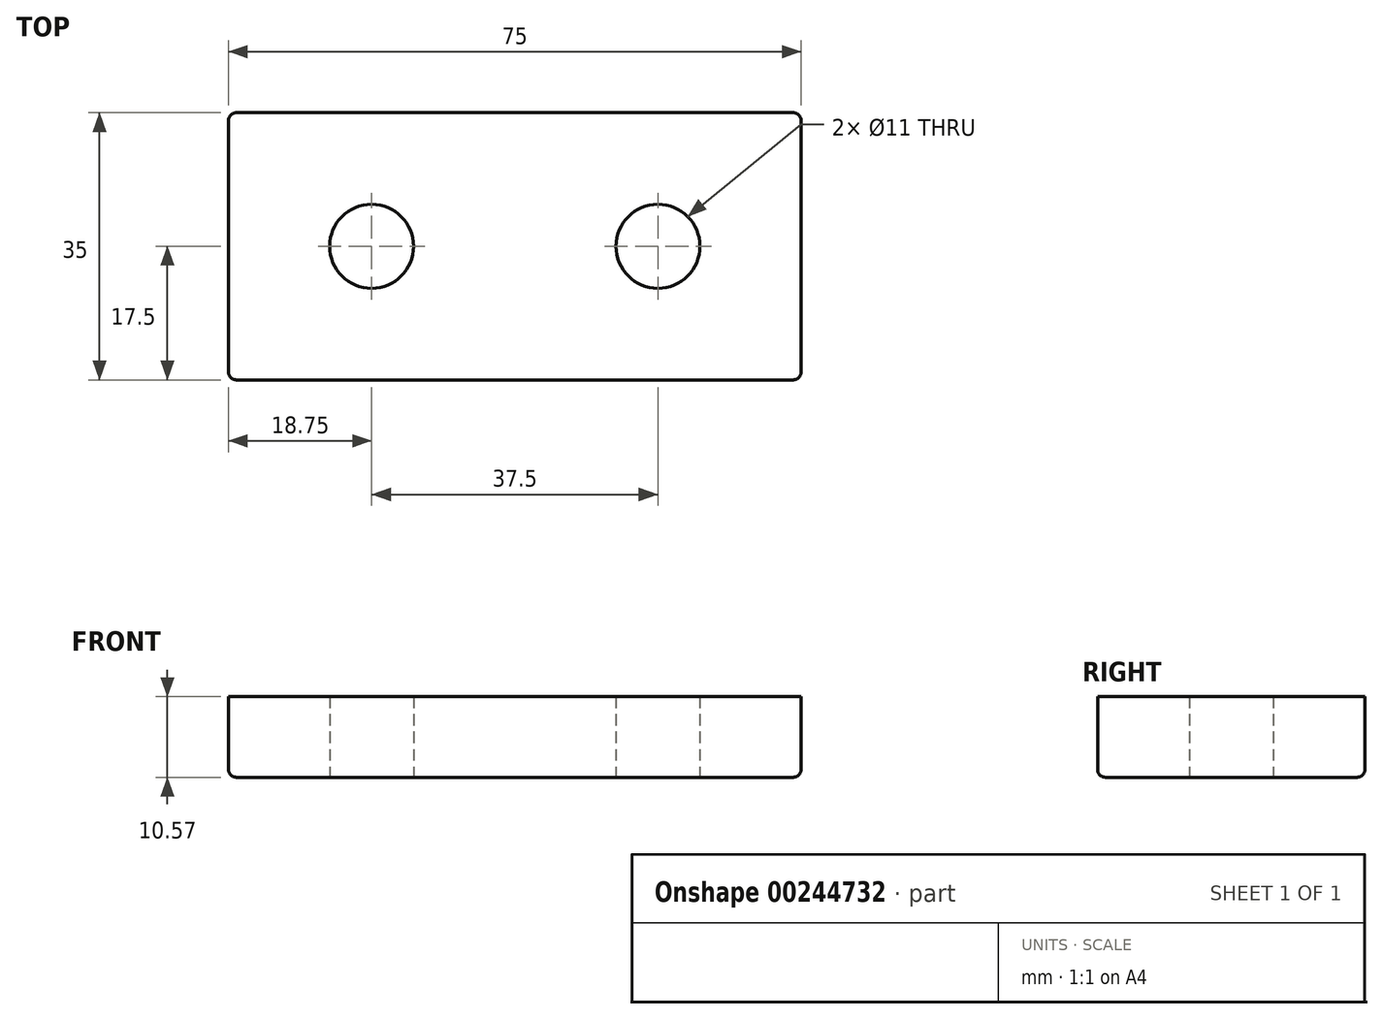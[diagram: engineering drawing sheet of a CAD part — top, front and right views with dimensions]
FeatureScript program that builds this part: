
annotation { "Feature Type Name" : "Feature", "Feature Type Description" : "" }
export const myFeature = defineFeature(function(context is Context, id is Id, definition is map)
    precondition{}
    {
        {
            var Q0;
            Q0=qCreatedBy(makeId("Top.planeOp"),FACE);
            var sketch = newSketch(context, id + "F0", { "sketchPlane" : qUnion([Q0])});
            skLineSegment(sketch, "E0.bottom", {"start": v(-37.5, 17.5) * mm, "end": v(37.5, 17.5) * mm});
            skLineSegment(sketch, "E0.top", {"start": v(-37.5, -17.5) * mm, "end": v(37.5, -17.5) * mm});
            skLineSegment(sketch, "E0.left", {"start": v(-37.5, 17.5) * mm, "end": v(-37.5, -17.5) * mm});
            skLineSegment(sketch, "E0.right", {"start": v(37.5, 17.5) * mm, "end": v(37.5, -17.5) * mm});
            skPoint(sketch, "E0.middle", {"position": v(0, 0) * mm});
            skLineSegment(sketch, "E1", {"start": v(-18.75, 0) * mm, "end": v(18.75, 0) * mm});
            skSolve(sketch);
        }
        {
            var Q0;
            Q0=makeQuery(id+"F0.imprint","IMPRINT",FACE,{"disambiguationData":[TD([[makeQuery(id+"F0.imprint","IMPRINT",EDGE,{"derivedFrom":sQuery(id+"F0.wireOp",EDGE,"E0.bottom")}),-1.0]])]});
            extrude(context, id + "F1", {"entities" : qUnion([Q0]), "depth" : 10.57 * mm});
        }
        {
            var Q0;
            Q0=sQuery(id+"F0.wireOp",VERTEX,"E1.start");
            var Q1;
            Q1=sQuery(id+"F0.wireOp",VERTEX,"E1.end");
            var Q2;
            Q2=makeQuery(id+"F1.opExtrude","SWEPT_BODY",BODY,{"disambiguationData":[OSD([sQuery(id+"F0.wireOp",EDGE,"E0.bottom"),sQuery(id+"F0.wireOp",EDGE,"E0.top"),sQuery(id+"F0.wireOp",EDGE,"E0.left"),sQuery(id+"F0.wireOp",EDGE,"E0.right")])]});
            hole(context, id + "F2", {"style" : HoleStyle.SIMPLE, "endStyle" : HoleEndStyle.THROUGH, "oppositeDirection" : true, "standardTappedOrClearance" : lookupTablePath({ "standard" : "ISO", "fit" : "Normal", "size" : "M10", "type" : "Clearance" }), "standardBlindInLast" : lookupTablePath({ "fit" : "Standard", "standard" : "ISO", "size" : "M10", "type" : "Clearance" }), "holeDiameter" : 11 * mm, "tappedDepth" : 12 * mm, "tapClearance" : 3, "locations" : qUnion([Q0, Q1]), "scope" : qUnion([Q2])});
        }
        {
            var Q0;
            Q0=makeQuery(id+"F1.opExtrude","CAP_EDGE",EDGE,{"disambiguationData":[OSD([sQuery(id+"F0.wireOp",EDGE,"E0.top")])],"isStart":true});
            var Q1;
            Q1=makeQuery(id+"F1.opExtrude","SWEPT_EDGE",EDGE,{"disambiguationData":[OSD([sQuery(id+"F0.wireOp",EDGE,"E0.top"),sQuery(id+"F0.wireOp",EDGE,"E0.left")])]});
            var Q2;
            Q2=makeQuery(id+"F1.opExtrude","SWEPT_EDGE",EDGE,{"disambiguationData":[OSD([sQuery(id+"F0.wireOp",EDGE,"E0.top"),sQuery(id+"F0.wireOp",EDGE,"E0.right")])]});
            var Q3;
            Q3=makeQuery(id+"F1.opExtrude","CAP_EDGE",EDGE,{"disambiguationData":[OSD([sQuery(id+"F0.wireOp",EDGE,"E0.right")])],"isStart":true});
            var Q4;
            Q4=makeQuery(id+"F1.opExtrude","CAP_EDGE",EDGE,{"disambiguationData":[OSD([sQuery(id+"F0.wireOp",EDGE,"E0.left")])],"isStart":true});
            var Q5;
            Q5=makeQuery(id+"F1.opExtrude","CAP_EDGE",EDGE,{"disambiguationData":[OSD([sQuery(id+"F0.wireOp",EDGE,"E0.bottom")])],"isStart":true});
            var Q6;
            Q6=makeQuery(id+"F1.opExtrude","SWEPT_EDGE",EDGE,{"disambiguationData":[OSD([sQuery(id+"F0.wireOp",EDGE,"E0.bottom"),sQuery(id+"F0.wireOp",EDGE,"E0.left")])]});
            var Q7;
            Q7=makeQuery(id+"F1.opExtrude","SWEPT_EDGE",EDGE,{"disambiguationData":[OSD([sQuery(id+"F0.wireOp",EDGE,"E0.bottom"),sQuery(id+"F0.wireOp",EDGE,"E0.right")])]});
            fillet(context, id + "F3", {"entities" : qUnion([Q0, Q1, Q2, Q3, Q4, Q5, Q6, Q7]), "radius" : 1 * mm, "tangentPropagation" : true, "allowEdgeOverflow" : false});
        }
    });
